# Revit family: xFaucet_Hands_Free-American_Standard-Beale-4931.380
name_source: partatom
category: Plumbing Fixtures
revit_build: Autodesk Revit 2014 (Build: 20130308_1515(x64)
units: mm (PartAtom-declared; Revit-internal decimal feet)

## types (1)
- 4931.380
    ADA Compliant = Yes
    Assembly Code = D2020300
    CW Connection = Yes
    CWFU = 1.5
    Default Elevation = 0"
    Description = Beale Pull-Down Kitchen Faucet With Selectronic Hands-Free Technology
    Finish = Metal-American Standard-002-Polished Chrome
    Flow Rate = 1.5 gpm (5.7L/min)
    HW Connection = Yes
    HWFU = 1.5
    Height = 17 9/16"
    Installation Type = Deck Mounted
    Length = 10 3/8"
    Manufacturer = American Standard
    Material = Metal-American Standard-002-Polished Chrome
    Model = 4931.380
    Price = Prices may vary. Please consult Manufacturer Representative for most up-to-date price list.
    Product Documentation Link = https://www.americanstandard-us.com
    Product Page URL = https://www.americanstandard-us.com
    Specification = Single control kitchen pull-down faucet shall feature a hands-free Selectronic sensor with sliding door, a high arc brass swivel spout with pull-down two-function spray, and metal lever handle. Shall also feature 35 mm washerless ceramic disc valve cartridge and flexible Stainless Steel supply hoses.
    URL = http://www.americanstandard-us.com
    Vent Connection = No
    WFU = 2
    Waste Connection = No
    Width = 1 1/2"

## geometry (parser evidence)
native form markers: Sweep x1
no freeform markers — native parametric forms only
